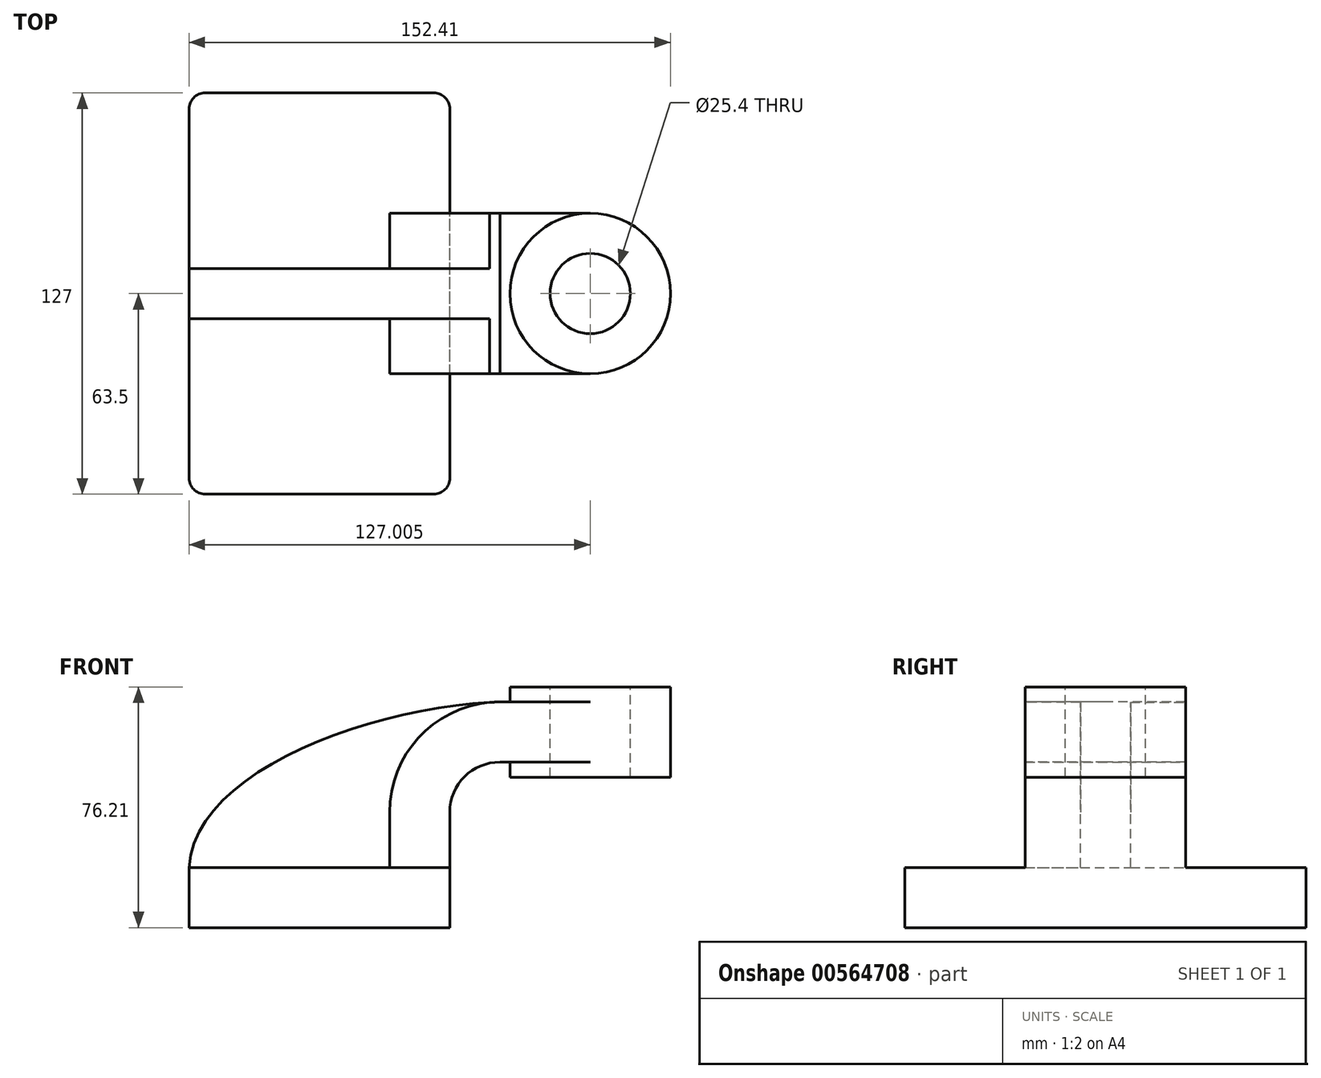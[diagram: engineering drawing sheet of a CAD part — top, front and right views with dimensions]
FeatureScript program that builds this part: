
annotation { "Feature Type Name" : "Feature", "Feature Type Description" : "" }
export const myFeature = defineFeature(function(context is Context, id is Id, definition is map)
    precondition{}
    {
        {
            var Q0;
            Q0=qCreatedBy(makeId("Front.planeOp"),FACE);
            var sketch = newSketch(context, id + "F0", { "sketchPlane" : qUnion([Q0])});
            skLineSegment(sketch, "E0.rect.bottom", {"start": v(-41.28, 9.52) * mm, "end": v(41.28, 9.52) * mm});
            skLineSegment(sketch, "E0.rect.top", {"start": v(-41.28, -9.52) * mm, "end": v(41.28, -9.52) * mm});
            skLineSegment(sketch, "E0.rect.left", {"start": v(-41.28, 9.52) * mm, "end": v(-41.28, -9.52) * mm});
            skLineSegment(sketch, "E0.rect.right", {"start": v(41.28, 9.52) * mm, "end": v(41.28, -9.52) * mm});
            skPoint(sketch, "E0.rect.middle", {"position": v(0, 0) * mm});
            skLineSegment(sketch, "E1", {"start": v(41.28, 9.52) * mm, "end": v(41.28, 27) * mm});
            skArc(sketch, "E2", {"start": v(41.28, 27) * mm, "mid": v(45.92, 38.23) * mm, "end": v(57.15, 42.88) * mm});
            skLineSegment(sketch, "E3", {"start": v(57.15, 42.88) * mm, "end": v(85.72, 42.88) * mm});
            skLineSegment(sketch, "E4.rect.bottom", {"start": v(60.32, 38.1) * mm, "end": v(111.12, 38.1) * mm});
            skLineSegment(sketch, "E4.rect.top", {"start": v(60.32, 66.68) * mm, "end": v(111.12, 66.68) * mm});
            skLineSegment(sketch, "E4.rect.left", {"start": v(60.32, 38.1) * mm, "end": v(60.32, 66.68) * mm});
            skLineSegment(sketch, "E4.rect.right", {"start": v(111.13, 38.1) * mm, "end": v(111.12, 66.68) * mm});
            skPoint(sketch, "E4.rect.middle", {"position": v(85.72, 52.39) * mm});
            skLineSegment(sketch, "E5.0", {"start": v(57.15, 61.93) * mm, "end": v(85.72, 61.93) * mm});
            skArc(sketch, "E5.1", {"start": v(22.23, 27) * mm, "mid": v(32.45, 51.7) * mm, "end": v(57.15, 61.93) * mm});
            skLineSegment(sketch, "E5.2", {"start": v(22.23, 9.52) * mm, "end": v(22.23, 27) * mm});
            skLineSegment(sketch, "E6", {"start": v(85.72, 38.1) * mm, "end": v(85.72, 66.68) * mm});
            skFitSpline(sketch, "E7", {"points": [v(-41.28, 9.53) * mm, v(57.15, 61.93) * mm], "startDerivative": vector(5.2, 92.34) * mm, "endDerivative": vector(120.92, 4.22) * mm});
            skSolve(sketch);
        }
        {
            var Q0;
            Q0=makeQuery(id+"F0.imprint","IMPRINT",FACE,{"disambiguationData":[TD([[makeQuery(id+"F0.imprint","IMPRINT",EDGE,{"derivedFrom":sQuery(id+"F0.wireOp",EDGE,"E0.rect.top")}),1.0]])]});
            extrude(context, id + "F1", {"entities" : qUnion([Q0]), "endBound" : BoundingType.SYMMETRIC, "depth" : 127 * mm});
        }
        {
            var Q0;
            {var subQ9=sQuery(id+"F0.wireOp",EDGE,"E1");Q0=makeQuery(id+"F0.imprint","IMPRINT",FACE,{"disambiguationData":[TD([[makeQuery(id+"F0.imprint","IMPRINT",EDGE,{"derivedFrom":subQ9}),1.0]])]});}
            var Q1;
            {var subQ0=sQuery(id+"F0.wireOp",EDGE,"E6");var subQ1=sQuery(id+"F0.wireOp",EDGE,"E3");var subQ2=makeQuery(id+"F0.imprint","INTERSECT",VERTEX,{"derivedFrom":[subQ1,subQ0]});Q1=makeQuery(id+"F0.imprint","IMPRINT",FACE,{"disambiguationData":[TD([[makeQuery(id+"F0.imprint","IMPRINT",EDGE,{"disambiguationData":[TD([[subQ2,1.0]])],"derivedFrom":subQ1}),1.0]])]});}
            extrude(context, id + "F2", {"entities" : qUnion([Q0, Q1]), "operationType" : NewBodyOperationType.ADD, "endBound" : BoundingType.SYMMETRIC, "depth" : 50.8 * mm});
        }
        {
            var Q0;
            {var subQ3=sQuery(id+"F0.wireOp",EDGE,"E5.2");Q0=makeQuery(id+"F0.imprint","IMPRINT",FACE,{"disambiguationData":[TD([[makeQuery(id+"F0.imprint","IMPRINT",EDGE,{"derivedFrom":subQ3}),1.0]])]});}
            extrude(context, id + "F3", {"entities" : qUnion([Q0]), "operationType" : NewBodyOperationType.ADD, "endBound" : BoundingType.SYMMETRIC, "depth" : 15.88 * mm});
        }
        {
            var Q0;
            {var subQ5=sQuery(id+"F0.wireOp",EDGE,"E4.rect.right");Q0=makeQuery(id+"F0.imprint","IMPRINT",FACE,{"disambiguationData":[TD([[makeQuery(id+"F0.imprint","IMPRINT",EDGE,{"derivedFrom":subQ5}),1.0]])]});}
            var Q1;
            Q1=sQuery(id+"F0.wireOp",EDGE,"E6");
            revolve(context, id + "F4", {"operationType" : NewBodyOperationType.ADD, "entities" : qUnion([Q0]), "axis" : qUnion([Q1]), "revolveType" : RevolveType.FULL});
        }
        {
            var Q0;
            Q0=makeQuery(id+"F1.opExtrude","CAP_EDGE",EDGE,{"disambiguationData":[OSD([sQuery(id+"F0.wireOp",EDGE,"E0.rect.right")])],"isStart":false});
            var Q1;
            Q1=makeQuery(id+"F1.opExtrude","CAP_EDGE",EDGE,{"disambiguationData":[OSD([sQuery(id+"F0.wireOp",EDGE,"E0.rect.left")])],"isStart":false});
            var Q2;
            Q2=makeQuery(id+"F1.opExtrude","CAP_EDGE",EDGE,{"disambiguationData":[OSD([sQuery(id+"F0.wireOp",EDGE,"E0.rect.right")])],"isStart":true});
            var Q3;
            Q3=makeQuery(id+"F1.opExtrude","CAP_EDGE",EDGE,{"disambiguationData":[OSD([sQuery(id+"F0.wireOp",EDGE,"E0.rect.left")])],"isStart":true});
            fillet(context, id + "F5", {"entities" : qUnion([Q0, Q1, Q2, Q3]), "radius" : 5.08 * mm, "tangentPropagation" : true, "allowEdgeOverflow" : false});
        }
        {
            var Q0;
            Q0=makeQuery(id+"F4.opRevolve","SWEPT_FACE",FACE,{"disambiguationData":[OSD([sQuery(id+"F0.wireOp",EDGE,"E4.rect.top")])]});
            var sketch = newSketch(context, id + "F6", { "sketchPlane" : qUnion([Q0])});
            skCircle(sketch, "E8", {"center": v(85.72, 0) * mm, "radius": 12.7 * mm});
            skSolve(sketch);
        }
        {
            var Q0;
            Q0=makeQuery(id+"F6.imprint","IMPRINT",FACE,{"disambiguationData":[TD([[makeQuery(id+"F6.imprint","IMPRINT",EDGE,{"derivedFrom":sQuery(id+"F6.wireOp",EDGE,"E8")}),1.0]])]});
            extrude(context, id + "F7", {"entities" : qUnion([Q0]), "operationType" : NewBodyOperationType.REMOVE, "endBound" : BoundingType.THROUGH_ALL, "oppositeDirection" : true, "depth" : 25.4 * mm, "offsetDistance" : 25.4 * mm});
        }
    });
